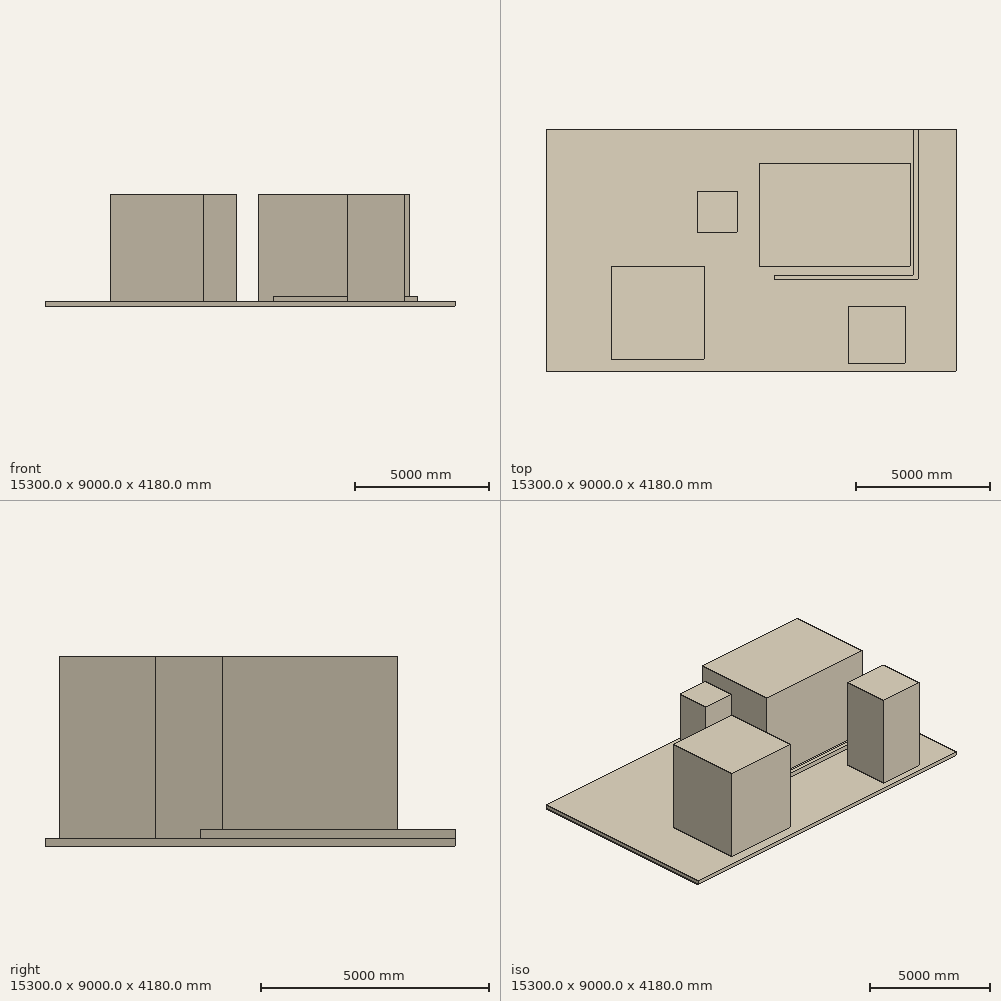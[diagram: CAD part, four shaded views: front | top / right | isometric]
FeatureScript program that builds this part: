
annotation { "Feature Type Name" : "Feature", "Feature Type Description" : "" }
export const myFeature = defineFeature(function(context is Context, id is Id, definition is map)
    precondition{}
    {
        {
            var Q0;
            Q0=qCreatedBy(makeId("Top.planeOp"),FACE);
            var sketch = newSketch(context, id + "F0", { "sketchPlane" : qUnion([Q0])});
            skLineSegment(sketch, "E0.bottom", {"start": v(-7650, -4500) * mm, "end": v(7650, -4500) * mm});
            skLineSegment(sketch, "E0.top", {"start": v(-7650, 4500) * mm, "end": v(7650, 4500) * mm});
            skLineSegment(sketch, "E0.left", {"start": v(-7650, -4500) * mm, "end": v(-7650, 4500) * mm});
            skLineSegment(sketch, "E0.right", {"start": v(7650, -4500) * mm, "end": v(7650, 4500) * mm});
            skPoint(sketch, "E0.middle", {"position": v(0, 0) * mm});
            skLineSegment(sketch, "E1.bottom", {"start": v(5750, -2080) * mm, "end": v(3630, -2080) * mm});
            skLineSegment(sketch, "E1.top", {"start": v(5750, -4200) * mm, "end": v(3630, -4200) * mm});
            skLineSegment(sketch, "E1.left", {"start": v(5750, -2080) * mm, "end": v(5750, -4200) * mm});
            skLineSegment(sketch, "E1.right", {"start": v(3630, -2080) * mm, "end": v(3630, -4200) * mm});
            skPoint(sketch, "E1.middle", {"position": v(4690, -3140) * mm});
            skLineSegment(sketch, "E2.bottom", {"start": v(-1740, -4050) * mm, "end": v(-5210, -4050) * mm});
            skLineSegment(sketch, "E2.top", {"start": v(-1740, -580) * mm, "end": v(-5210, -580) * mm});
            skLineSegment(sketch, "E2.left", {"start": v(-1740, -4050) * mm, "end": v(-1740, -580) * mm});
            skLineSegment(sketch, "E2.right", {"start": v(-5210, -4050) * mm, "end": v(-5210, -580) * mm});
            skPoint(sketch, "E2.middle", {"position": v(-3475, -2315) * mm});
            skLineSegment(sketch, "E3.bottom", {"start": v(-510, 680) * mm, "end": v(-2030, 680) * mm});
            skLineSegment(sketch, "E3.top", {"start": v(-510, 2200) * mm, "end": v(-2030, 2200) * mm});
            skLineSegment(sketch, "E3.left", {"start": v(-510, 680) * mm, "end": v(-510, 2200) * mm});
            skLineSegment(sketch, "E3.right", {"start": v(-2030, 680) * mm, "end": v(-2030, 2200) * mm});
            skPoint(sketch, "E3.middle", {"position": v(-1270, 1440) * mm});
            skLineSegment(sketch, "E4", {"start": v(6220, 4500) * mm, "end": v(6220, -1100) * mm});
            skLineSegment(sketch, "E5", {"start": v(6220, -1100) * mm, "end": v(870, -1100) * mm});
            skLineSegment(sketch, "E6", {"start": v(870, -1100) * mm, "end": v(870, -920) * mm});
            skLineSegment(sketch, "E7.1", {"start": v(6040, -920) * mm, "end": v(1050, -920) * mm});
            skLineSegment(sketch, "E7.2", {"start": v(6040, 4500) * mm, "end": v(6040, -920) * mm});
            skLineSegment(sketch, "E8", {"start": v(1050, -920) * mm, "end": v(870, -920) * mm});
            skLineSegment(sketch, "E9.bottom", {"start": v(5950, -610) * mm, "end": v(305, -610) * mm});
            skLineSegment(sketch, "E9.top", {"start": v(5950, 3230) * mm, "end": v(305, 3230) * mm});
            skLineSegment(sketch, "E9.left", {"start": v(5950, -610) * mm, "end": v(5950, 3230) * mm});
            skLineSegment(sketch, "E9.right", {"start": v(305, -610) * mm, "end": v(305, 3230) * mm});
            skPoint(sketch, "E9.middle", {"position": v(3127.5, 1310) * mm});
            skSolve(sketch);
        }
        {
            var Q0;
            Q0=makeQuery(id+"F0.imprint","IMPRINT",FACE,{"disambiguationData":[TD([[makeQuery(id+"F0.imprint","IMPRINT",EDGE,{"derivedFrom":sQuery(id+"F0.wireOp",EDGE,"E0.bottom")}),1.0]])]});
            var Q1;
            Q1=makeQuery(id+"F0.imprint","IMPRINT",FACE,{"disambiguationData":[TD([[makeQuery(id+"F0.imprint","IMPRINT",EDGE,{"derivedFrom":sQuery(id+"F0.wireOp",EDGE,"fD09KaBE-grEl-lVdx-jNL6-XS2ACUkGUNsk.bottom")}),1.0]])]});
            var Q2;
            {var subQ0=sQuery(id+"F0.wireOp",EDGE,"E4");Q2=makeQuery(id+"F0.imprint","IMPRINT",FACE,{"disambiguationData":[TD([[makeQuery(id+"F0.imprint","IMPRINT",EDGE,{"derivedFrom":subQ0}),-1.0]])]});}
            var Q3;
            Q3=makeQuery(id+"F0.imprint","IMPRINT",FACE,{"disambiguationData":[TD([[makeQuery(id+"F0.imprint","IMPRINT",EDGE,{"derivedFrom":sQuery(id+"F0.wireOp",EDGE,"E2.bottom")}),-1.0]])]});
            var Q4;
            Q4=makeQuery(id+"F0.imprint","IMPRINT",FACE,{"disambiguationData":[TD([[makeQuery(id+"F0.imprint","IMPRINT",EDGE,{"derivedFrom":sQuery(id+"F0.wireOp",EDGE,"E3.bottom")}),-1.0]])]});
            var Q5;
            Q5=makeQuery(id+"F0.imprint","IMPRINT",FACE,{"disambiguationData":[TD([[makeQuery(id+"F0.imprint","IMPRINT",EDGE,{"derivedFrom":sQuery(id+"F0.wireOp",EDGE,"Og1JvU4z-OaGR-lbiX-x8T8-D1ppF5jEQ3Tk.bottom")}),-1.0]])]});
            var Q6;
            Q6=makeQuery(id+"F0.imprint","IMPRINT",FACE,{"disambiguationData":[TD([[makeQuery(id+"F0.imprint","IMPRINT",EDGE,{"derivedFrom":sQuery(id+"F0.wireOp",EDGE,"fD09KaBE-grEl-lVdx-jNL6-XS2ACUkGUNsk.bottom")}),-1.0]])]});
            var Q7;
            Q7=makeQuery(id+"F0.imprint","IMPRINT",FACE,{"disambiguationData":[TD([[makeQuery(id+"F0.imprint","IMPRINT",EDGE,{"derivedFrom":sQuery(id+"F0.wireOp",EDGE,"E1.bottom")}),1.0]])]});
            var Q8;
            Q8=makeQuery(id+"F0.imprint","IMPRINT",FACE,{"disambiguationData":[TD([[makeQuery(id+"F0.imprint","IMPRINT",EDGE,{"derivedFrom":sQuery(id+"F0.wireOp",EDGE,"D4kSk7Ny-QVZ7-tqfS-EeB5-YYYW7lg6BN4g.bottom")}),-1.0]])]});
            var Q9;
            Q9=makeQuery(id+"F0.imprint","IMPRINT",FACE,{"disambiguationData":[TD([[makeQuery(id+"F0.imprint","IMPRINT",EDGE,{"derivedFrom":sQuery(id+"F0.wireOp",EDGE,"E9.bottom")}),-1.0]])]});
            extrude(context, id + "F1", {"entities" : qUnion([Q0, Q1, Q2, Q3, Q4, Q5, Q6, Q7, Q8, Q9]), "oppositeDirection" : true, "depth" : 180 * mm});
        }
        {
            var Q0;
            Q0=makeQuery(id+"F0.imprint","IMPRINT",FACE,{"disambiguationData":[TD([[makeQuery(id+"F0.imprint","IMPRINT",EDGE,{"derivedFrom":sQuery(id+"F0.wireOp",EDGE,"E2.bottom")}),-1.0]])]});
            var Q1;
            Q1=makeQuery(id+"F0.imprint","IMPRINT",FACE,{"disambiguationData":[TD([[makeQuery(id+"F0.imprint","IMPRINT",EDGE,{"derivedFrom":sQuery(id+"F0.wireOp",EDGE,"E3.bottom")}),-1.0]])]});
            var Q2;
            Q2=makeQuery(id+"F0.imprint","IMPRINT",FACE,{"disambiguationData":[TD([[makeQuery(id+"F0.imprint","IMPRINT",EDGE,{"derivedFrom":sQuery(id+"F0.wireOp",EDGE,"Og1JvU4z-OaGR-lbiX-x8T8-D1ppF5jEQ3Tk.bottom")}),-1.0]])]});
            var Q3;
            Q3=makeQuery(id+"F0.imprint","IMPRINT",FACE,{"disambiguationData":[TD([[makeQuery(id+"F0.imprint","IMPRINT",EDGE,{"derivedFrom":sQuery(id+"F0.wireOp",EDGE,"fD09KaBE-grEl-lVdx-jNL6-XS2ACUkGUNsk.bottom")}),-1.0]])]});
            var Q4;
            Q4=makeQuery(id+"F0.imprint","IMPRINT",FACE,{"disambiguationData":[TD([[makeQuery(id+"F0.imprint","IMPRINT",EDGE,{"derivedFrom":sQuery(id+"F0.wireOp",EDGE,"E1.bottom")}),1.0]])]});
            var Q5;
            Q5=makeQuery(id+"F0.imprint","IMPRINT",FACE,{"disambiguationData":[TD([[makeQuery(id+"F0.imprint","IMPRINT",EDGE,{"derivedFrom":sQuery(id+"F0.wireOp",EDGE,"D4kSk7Ny-QVZ7-tqfS-EeB5-YYYW7lg6BN4g.bottom")}),-1.0]])]});
            var Q6;
            Q6=makeQuery(id+"F0.imprint","IMPRINT",FACE,{"disambiguationData":[TD([[makeQuery(id+"F0.imprint","IMPRINT",EDGE,{"derivedFrom":sQuery(id+"F0.wireOp",EDGE,"E9.bottom")}),-1.0]])]});
            extrude(context, id + "F2", {"entities" : qUnion([Q0, Q1, Q2, Q3, Q4, Q5, Q6]), "operationType" : NewBodyOperationType.ADD, "depth" : 4000 * mm});
        }
        {
            var Q0;
            {var subQ0=sQuery(id+"F0.wireOp",EDGE,"E4");Q0=makeQuery(id+"F0.imprint","IMPRINT",FACE,{"disambiguationData":[TD([[makeQuery(id+"F0.imprint","IMPRINT",EDGE,{"derivedFrom":subQ0}),-1.0]])]});}
            extrude(context, id + "F3", {"entities" : qUnion([Q0]), "operationType" : NewBodyOperationType.ADD, "depth" : 200 * mm});
        }
    });
